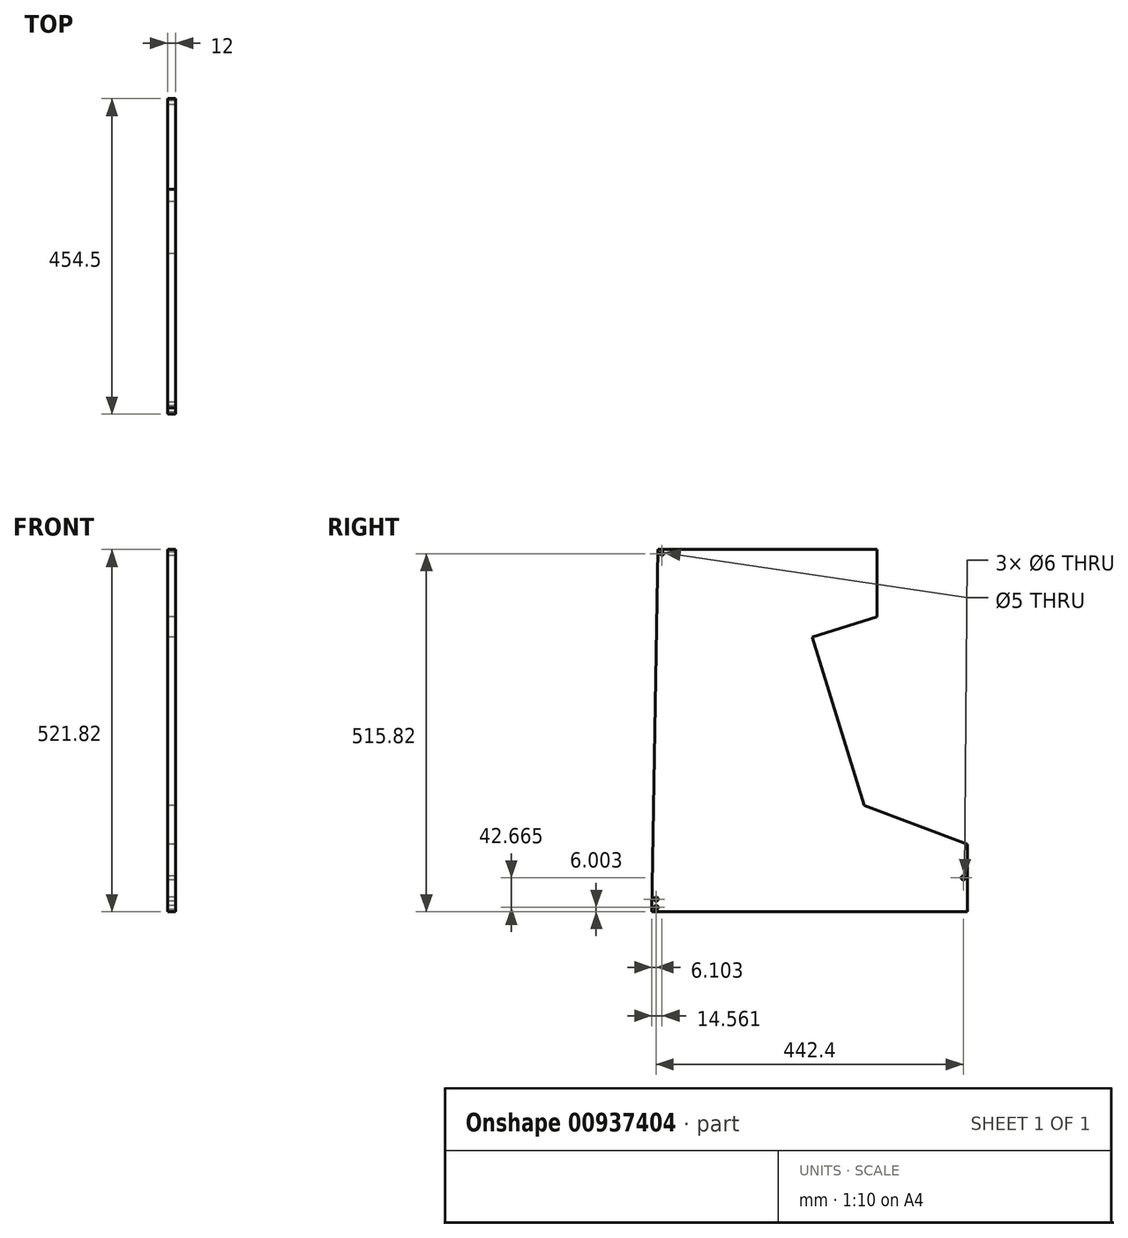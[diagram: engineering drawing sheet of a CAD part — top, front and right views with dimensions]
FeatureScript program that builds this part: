
annotation { "Feature Type Name" : "Feature", "Feature Type Description" : "" }
export const myFeature = defineFeature(function(context is Context, id is Id, definition is map)
    precondition{}
    {
        {
            var Q0;
            Q0=qCreatedBy(makeId("Right.planeOp"),FACE);
            var sketch = newSketch(context, id + "F0", { "sketchPlane" : qUnion([Q0])});
            skLineSegment(sketch, "E0.top", {"start": v(343.45, -931.38) * mm, "end": v(797.95, -931.38) * mm});
            skLineSegment(sketch, "E1", {"start": v(797.95, -931.38) * mm, "end": v(797.95, -834.05) * mm});
            skLineSegment(sketch, "E2", {"start": v(797.95, -834.05) * mm, "end": v(649.29, -778.29) * mm});
            skPoint(sketch, "E2.endSnap0", {"position": v(742.2, -778.29) * mm});
            skPoint(sketch, "E3.orphan", {"position": v(686.43, -722.53) * mm});
            skLineSegment(sketch, "E4", {"start": v(649.29, -778.29) * mm, "end": v(574.5, -535.54) * mm});
            skLineSegment(sketch, "E5", {"start": v(574.5, -535.54) * mm, "end": v(667.52, -506.89) * mm});
            skPoint(sketch, "E6.end.orphan", {"position": v(323.35, -412.94) * mm});
            skPoint(sketch, "E7.end.orphan", {"position": v(667.52, -412.94) * mm});
            skLineSegment(sketch, "E8", {"start": v(352.11, -409.56) * mm, "end": v(667.52, -409.56) * mm});
            skLineSegment(sketch, "E9", {"start": v(667.52, -409.56) * mm, "end": v(667.52, -506.89) * mm});
            skPoint(sketch, "E10.end.orphan", {"position": v(343.45, -409.56) * mm});
            skLineSegment(sketch, "E11", {"start": v(352.11, -409.56) * mm, "end": v(343.45, -931.38) * mm});
            skPoint(sketch, "E12.end.orphan", {"position": v(364.1, -529.62) * mm});
            skPoint(sketch, "E13.orphan", {"position": v(355.65, -931.38) * mm});
            skPoint(sketch, "E14.orphan", {"position": v(352.11, -421.36) * mm});
            skPoint(sketch, "E15.end.orphan", {"position": v(667.52, -421.36) * mm});
            skPoint(sketch, "E16.center.orphan", {"position": v(364.1, -421.56) * mm});
            skCircle(sketch, "E17", {"center": v(358.01, -415.56) * mm, "radius": 2.5 * mm});
            skCircle(sketch, "E18", {"center": v(349.55, -925.38) * mm, "radius": 3 * mm});
            skCircle(sketch, "E19", {"center": v(791.95, -882.71) * mm, "radius": 3 * mm});
            skPoint(sketch, "E20.start.orphan", {"position": v(797.95, -882.71) * mm});
            skCircle(sketch, "E21", {"center": v(349.55, -913.38) * mm, "radius": 3 * mm});
            skSolve(sketch);
        }
        {
            var Q0;
            Q0 = qSketchRegion(id + "F0", true);
            extrude(context, id + "F1", {"entities" : qUnion([Q0]), "depth" : 12 * mm, "offsetDistance" : 25 * mm});
        }
    });
